# Revit family: US23-4100-08 Powerswing Single Door Push App Pedestrian Rev B
name_source: partatom
category: Doors
revit_build: Autodesk Revit MEP 2014 (Build: 20130308_1515(x64)
units: mm (PartAtom-declared; Revit-internal decimal feet)

## types (2) — shared parameters
Analytic Construction = <None>
Depth (mm) = 0"
Disclaimer = Consult product specification for sensors to comply with ANSI A156.10
Function = Interior
Height (mm) = 0"
Material main = Aluminium
Material secondary = Aluminium
Midrail = Yes
Product data url = http://besam-na.bimobject.com
Wall Closure = By host
Width (mm) = 0"

## per-type parameters (varying)
| type | BIMobject category | Date of publishing | Depth | Edition number | IFC Classification | Manufacturer name | Midrail Width | Nominal height | Nominal width | Product Guid | Product SKU | Product family | Product group | QR code | UNSPSC Code | Uniclass 1.4 Code | Uniclass 1.4 Description | Weight Net (Kg) |
| Midrail 6'' | Swing Doors | 2015-02-23 | 0.00 | 1 | Door | Besam-North America | 6" | 0.00 | 0.00 | 8f5fc71c-b491-450f-9aa1-f466428b75e0 | PowerSwing_SM | Swing | Surface Mount | http://besam-na.bimobject.com | 30171511 | L81323 | Swings | 0 |
| Midrail 3'' |  |  |  |  |  |  | 3" |  |  |  |  |  |  |  |  |  |  |  |

## geometry (parser evidence)
native form markers: Blend x4, Sweep x2
no freeform markers — native parametric forms only
